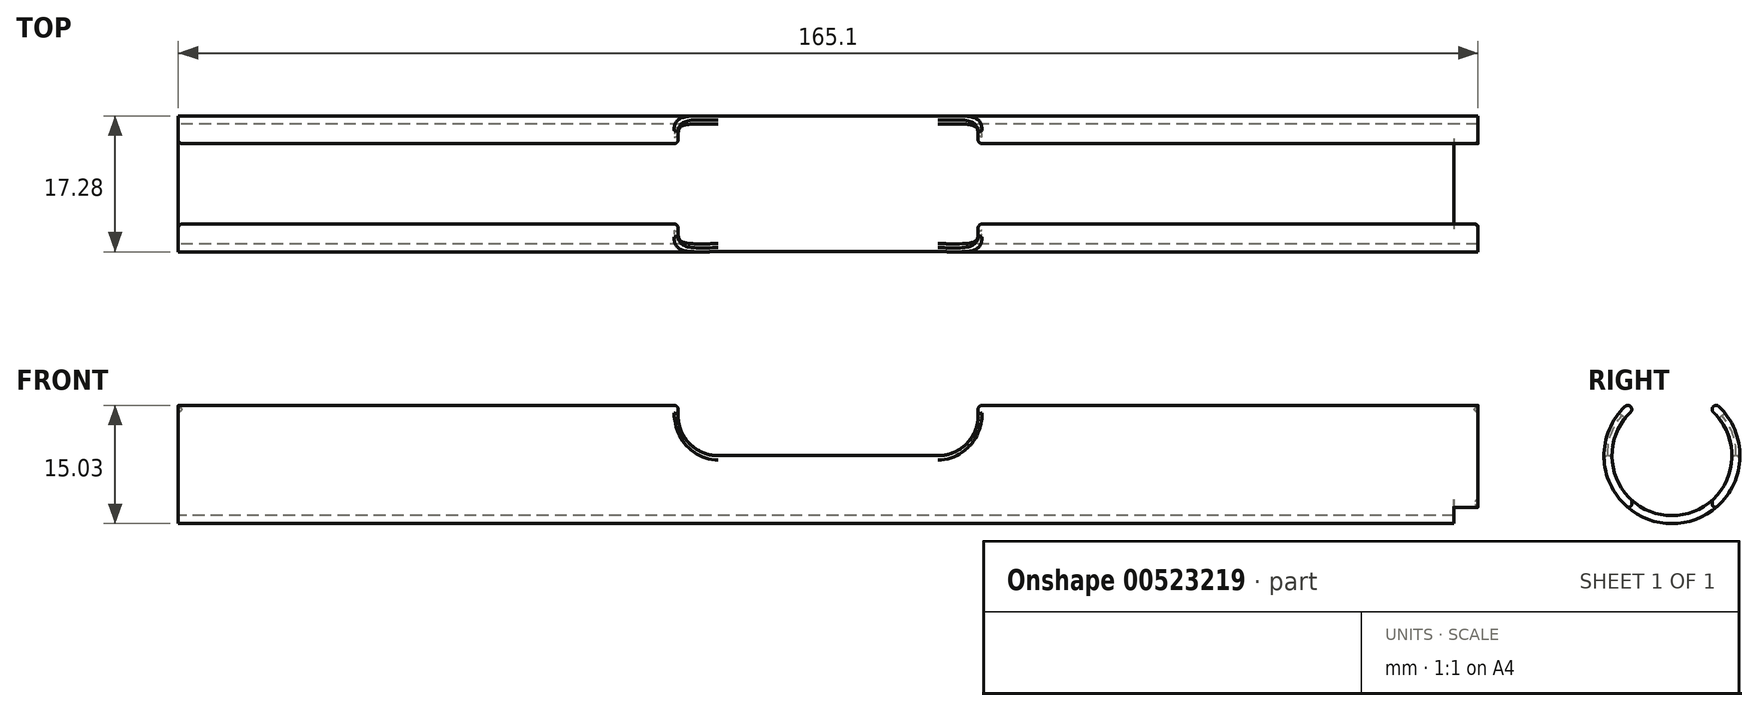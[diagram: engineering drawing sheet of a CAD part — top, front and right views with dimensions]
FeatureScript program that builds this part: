
annotation { "Feature Type Name" : "Feature", "Feature Type Description" : "" }
export const myFeature = defineFeature(function(context is Context, id is Id, definition is map)
    precondition{}
    {
        {
            var Q0;
            Q0=qCreatedBy(makeId("Right.planeOp"),FACE);
            var sketch = newSketch(context, id + "F0", { "sketchPlane" : qUnion([Q0])});
            skArc(sketch, "E0", {"start": v(-5.1, 6.97) * mm, "mid": v(0, -8.64) * mm, "end": v(5.1, 6.97) * mm});
            skArc(sketch, "E1", {"start": v(-5.1, 5.66) * mm, "mid": v(0, -7.62) * mm, "end": v(5.1, 5.66) * mm});
            skLineSegment(sketch, "E2", {"start": v(-5.1, 6.97) * mm, "end": v(-5.1, 5.66) * mm});
            skLineSegment(sketch, "E3", {"start": v(5.1, 6.97) * mm, "end": v(5.1, 5.66) * mm});
            skSolve(sketch);
        }
        {
            var Q0;
            Q0=makeQuery(id+"F0.imprint","IMPRINT",FACE,{"disambiguationData":[TD([[makeQuery(id+"F0.imprint","IMPRINT",EDGE,{"derivedFrom":sQuery(id+"F0.wireOp",EDGE,"E0")}),1.0]])]});
            extrude(context, id + "F1", {"entities" : qUnion([Q0]), "depth" : 165.1 * mm, "offsetDistance" : 25.4 * mm});
        }
        {
            var Q0;
            Q0=qCreatedBy(makeId("Front.planeOp"),FACE);
            var sketch = newSketch(context, id + "F2", { "sketchPlane" : qUnion([Q0])});
            skLineSegment(sketch, "E4", {"start": v(63.5, 8.64) * mm, "end": v(63.5, 0) * mm});
            skLineSegment(sketch, "E5", {"start": v(101.6, 8.64) * mm, "end": v(101.6, 0) * mm});
            skLineSegment(sketch, "E6", {"start": v(63.5, 8.64) * mm, "end": v(101.6, 8.64) * mm});
            skPoint(sketch, "E7.orphan", {"position": v(104.85, 8.64) * mm});
            skPoint(sketch, "E8.orphan", {"position": v(104.85, 0) * mm});
            skPoint(sketch, "E9.orphan", {"position": v(101.6, -19.63) * mm});
            skPoint(sketch, "E10.orphan", {"position": v(63.5, -19.63) * mm});
            skLineSegment(sketch, "E11", {"start": v(63.5, 0) * mm, "end": v(101.6, 0) * mm});
            skSolve(sketch);
        }
        {
            var Q0;
            Q0 = qSketchRegion(id + "F2", true);
            extrude(context, id + "F3", {"entities" : qUnion([Q0]), "operationType" : NewBodyOperationType.REMOVE, "endBound" : BoundingType.SYMMETRIC, "depth" : 25.4 * mm, "offsetDistance" : 25.4 * mm});
        }
        {
            var Q0;
            Q0=makeQuery(id+"F3.boolean.opBoolean","COPY",EDGE,{"disambiguationData":[OD(1.0)],"derivedFrom":makeQuery(id+"F3.opExtrude","SWEPT_EDGE",EDGE,{"disambiguationData":[OSD([sQuery(id+"F2.wireOp",EDGE,"E4"),sQuery(id+"F2.wireOp",EDGE,"E11")])]})});
            var Q1;
            Q1=makeQuery(id+"F3.boolean.opBoolean","COPY",EDGE,{"disambiguationData":[OD(0.0)],"derivedFrom":makeQuery(id+"F3.opExtrude","SWEPT_EDGE",EDGE,{"disambiguationData":[OSD([sQuery(id+"F2.wireOp",EDGE,"E4"),sQuery(id+"F2.wireOp",EDGE,"E11")])]})});
            var Q2;
            Q2=makeQuery(id+"F3.boolean.opBoolean","COPY",EDGE,{"disambiguationData":[OD(1.0)],"derivedFrom":makeQuery(id+"F3.opExtrude","SWEPT_EDGE",EDGE,{"disambiguationData":[OSD([sQuery(id+"F2.wireOp",EDGE,"E5"),sQuery(id+"F2.wireOp",EDGE,"E11")])]})});
            var Q3;
            Q3=makeQuery(id+"F3.boolean.opBoolean","COPY",EDGE,{"disambiguationData":[OD(0.0)],"derivedFrom":makeQuery(id+"F3.opExtrude","SWEPT_EDGE",EDGE,{"disambiguationData":[OSD([sQuery(id+"F2.wireOp",EDGE,"E5"),sQuery(id+"F2.wireOp",EDGE,"E11")])]})});
            fillet(context, id + "F4", {"entities" : qUnion([Q0, Q1, Q2, Q3]), "radius" : 5.08 * mm, "tangentPropagation" : true, "allowEdgeOverflow" : false});
        }
        {
            var Q0;
            Q0=makeQuery(id+"F3.boolean.opBoolean","INTERSECT",EDGE,{"derivedFrom":[makeQuery(id+"F1.opExtrude","SWEPT_FACE",FACE,{"disambiguationData":[OSD([sQuery(id+"F0.wireOp",EDGE,"E2")])]}),makeQuery(id+"F3.opExtrude","SWEPT_FACE",FACE,{"disambiguationData":[OSD([sQuery(id+"F2.wireOp",EDGE,"E4")])]})]});
            var Q1;
            Q1=makeQuery(id+"F3.boolean.opBoolean","INTERSECT",EDGE,{"derivedFrom":[makeQuery(id+"F1.opExtrude","SWEPT_FACE",FACE,{"disambiguationData":[OSD([sQuery(id+"F0.wireOp",EDGE,"E3")])]}),makeQuery(id+"F3.opExtrude","SWEPT_FACE",FACE,{"disambiguationData":[OSD([sQuery(id+"F2.wireOp",EDGE,"E4")])]})]});
            var Q2;
            {var subQ0=sQuery(id+"F0.wireOp",EDGE,"E2");var subQ1=sQuery(id+"F0.wireOp",EDGE,"E1");Q2=makeQuery(id+"F3.boolean.opBoolean","SPLIT",EDGE,{"disambiguationData":[TD([makeQuery(id+"F3.opExtrude","SWEPT_FACE",FACE,{"disambiguationData":[OSD([sQuery(id+"F2.wireOp",EDGE,"E4")])]})])],"derivedFrom":makeQuery(id+"F1.opExtrude","SWEPT_EDGE",EDGE,{"disambiguationData":[OSD([subQ1,subQ0])]})});}
            var Q3;
            Q3=makeQuery(id+"F1.opExtrude","CAP_EDGE",EDGE,{"disambiguationData":[OSD([sQuery(id+"F0.wireOp",EDGE,"E2")])],"isStart":true});
            var Q4;
            {var subQ0=sQuery(id+"F0.wireOp",EDGE,"E3");var subQ1=sQuery(id+"F0.wireOp",EDGE,"E1");Q4=makeQuery(id+"F3.boolean.opBoolean","SPLIT",EDGE,{"disambiguationData":[TD([makeQuery(id+"F3.opExtrude","SWEPT_FACE",FACE,{"disambiguationData":[OSD([sQuery(id+"F2.wireOp",EDGE,"E4")])]})])],"derivedFrom":makeQuery(id+"F1.opExtrude","SWEPT_EDGE",EDGE,{"disambiguationData":[OSD([subQ1,subQ0])]})});}
            var Q5;
            Q5=makeQuery(id+"F1.opExtrude","CAP_EDGE",EDGE,{"disambiguationData":[OSD([sQuery(id+"F0.wireOp",EDGE,"E3")])],"isStart":true});
            var Q6;
            {var subQ0=sQuery(id+"F0.wireOp",EDGE,"E2");var subQ1=sQuery(id+"F0.wireOp",EDGE,"E1");Q6=makeQuery(id+"F3.boolean.opBoolean","SPLIT",EDGE,{"disambiguationData":[TD([makeQuery(id+"F3.opExtrude","SWEPT_FACE",FACE,{"disambiguationData":[OSD([sQuery(id+"F2.wireOp",EDGE,"E5")])]})])],"derivedFrom":makeQuery(id+"F1.opExtrude","SWEPT_EDGE",EDGE,{"disambiguationData":[OSD([subQ1,subQ0])]})});}
            var Q7;
            Q7=makeQuery(id+"F3.boolean.opBoolean","INTERSECT",EDGE,{"derivedFrom":[makeQuery(id+"F1.opExtrude","SWEPT_FACE",FACE,{"disambiguationData":[OSD([sQuery(id+"F0.wireOp",EDGE,"E2")])]}),makeQuery(id+"F3.opExtrude","SWEPT_FACE",FACE,{"disambiguationData":[OSD([sQuery(id+"F2.wireOp",EDGE,"E5")])]})]});
            var Q8;
            Q8=makeQuery(id+"F3.boolean.opBoolean","INTERSECT",EDGE,{"derivedFrom":[makeQuery(id+"F1.opExtrude","SWEPT_FACE",FACE,{"disambiguationData":[OSD([sQuery(id+"F0.wireOp",EDGE,"E3")])]}),makeQuery(id+"F3.opExtrude","SWEPT_FACE",FACE,{"disambiguationData":[OSD([sQuery(id+"F2.wireOp",EDGE,"E5")])]})]});
            var Q9;
            {var subQ0=sQuery(id+"F0.wireOp",EDGE,"E3");var subQ1=sQuery(id+"F0.wireOp",EDGE,"E1");Q9=makeQuery(id+"F3.boolean.opBoolean","SPLIT",EDGE,{"disambiguationData":[TD([makeQuery(id+"F3.opExtrude","SWEPT_FACE",FACE,{"disambiguationData":[OSD([sQuery(id+"F2.wireOp",EDGE,"E5")])]})])],"derivedFrom":makeQuery(id+"F1.opExtrude","SWEPT_EDGE",EDGE,{"disambiguationData":[OSD([subQ1,subQ0])]})});}
            var Q10;
            Q10=makeQuery(id+"F3.boolean.opBoolean","INTERSECT",EDGE,{"disambiguationData":[OD(1.0)],"derivedFrom":[makeQuery(id+"F1.opExtrude","SWEPT_FACE",FACE,{"disambiguationData":[OSD([sQuery(id+"F0.wireOp",EDGE,"E1")])]}),makeQuery(id+"F3.opExtrude","SWEPT_FACE",FACE,{"disambiguationData":[OSD([sQuery(id+"F2.wireOp",EDGE,"E5")])]})]});
            var Q11;
            Q11=makeQuery(id+"F1.opExtrude","CAP_EDGE",EDGE,{"disambiguationData":[OSD([sQuery(id+"F0.wireOp",EDGE,"E2")])],"isStart":false});
            var Q12;
            Q12=makeQuery(id+"F1.opExtrude","CAP_EDGE",EDGE,{"disambiguationData":[OSD([sQuery(id+"F0.wireOp",EDGE,"E3")])],"isStart":false});
            var Q13;
            {var subQ0=sQuery(id+"F0.wireOp",EDGE,"E0");var subQ1=sQuery(id+"F0.wireOp",EDGE,"E2");Q13=makeQuery(id+"F3.boolean.opBoolean","SPLIT",EDGE,{"disambiguationData":[TD([makeQuery(id+"F3.opExtrude","SWEPT_FACE",FACE,{"disambiguationData":[OSD([sQuery(id+"F2.wireOp",EDGE,"E5")])]})])],"derivedFrom":makeQuery(id+"F1.opExtrude","SWEPT_EDGE",EDGE,{"disambiguationData":[OSD([subQ0,subQ1])]})});}
            var Q14;
            {var subQ0=sQuery(id+"F0.wireOp",EDGE,"E0");var subQ1=sQuery(id+"F0.wireOp",EDGE,"E3");Q14=makeQuery(id+"F3.boolean.opBoolean","SPLIT",EDGE,{"disambiguationData":[TD([makeQuery(id+"F3.opExtrude","SWEPT_FACE",FACE,{"disambiguationData":[OSD([sQuery(id+"F2.wireOp",EDGE,"E5")])]})])],"derivedFrom":makeQuery(id+"F1.opExtrude","SWEPT_EDGE",EDGE,{"disambiguationData":[OSD([subQ0,subQ1])]})});}
            var Q15;
            Q15=makeQuery(id+"F3.boolean.opBoolean","INTERSECT",EDGE,{"disambiguationData":[OD(0.0)],"derivedFrom":[makeQuery(id+"F1.opExtrude","SWEPT_FACE",FACE,{"disambiguationData":[OSD([sQuery(id+"F0.wireOp",EDGE,"E1")])]}),makeQuery(id+"F3.opExtrude","SWEPT_FACE",FACE,{"disambiguationData":[OSD([sQuery(id+"F2.wireOp",EDGE,"E5")])]})]});
            var Q16;
            {var subQ0=sQuery(id+"F0.wireOp",EDGE,"E0");var subQ1=sQuery(id+"F0.wireOp",EDGE,"E2");Q16=makeQuery(id+"F3.boolean.opBoolean","SPLIT",EDGE,{"disambiguationData":[TD([makeQuery(id+"F3.opExtrude","SWEPT_FACE",FACE,{"disambiguationData":[OSD([sQuery(id+"F2.wireOp",EDGE,"E4")])]})])],"derivedFrom":makeQuery(id+"F1.opExtrude","SWEPT_EDGE",EDGE,{"disambiguationData":[OSD([subQ0,subQ1])]})});}
            var Q17;
            Q17=makeQuery(id+"F3.boolean.opBoolean","INTERSECT",EDGE,{"disambiguationData":[OD(0.0)],"derivedFrom":[makeQuery(id+"F1.opExtrude","SWEPT_FACE",FACE,{"disambiguationData":[OSD([sQuery(id+"F0.wireOp",EDGE,"E0")])]}),makeQuery(id+"F3.opExtrude","SWEPT_FACE",FACE,{"disambiguationData":[OSD([sQuery(id+"F2.wireOp",EDGE,"E4")])]})]});
            var Q18;
            {var subQ0=sQuery(id+"F0.wireOp",EDGE,"E0");var subQ1=sQuery(id+"F0.wireOp",EDGE,"E3");Q18=makeQuery(id+"F3.boolean.opBoolean","SPLIT",EDGE,{"disambiguationData":[TD([makeQuery(id+"F3.opExtrude","SWEPT_FACE",FACE,{"disambiguationData":[OSD([sQuery(id+"F2.wireOp",EDGE,"E4")])]})])],"derivedFrom":makeQuery(id+"F1.opExtrude","SWEPT_EDGE",EDGE,{"disambiguationData":[OSD([subQ0,subQ1])]})});}
            var Q19;
            Q19=makeQuery(id+"F3.boolean.opBoolean","INTERSECT",EDGE,{"disambiguationData":[OD(1.0)],"derivedFrom":[makeQuery(id+"F1.opExtrude","SWEPT_FACE",FACE,{"disambiguationData":[OSD([sQuery(id+"F0.wireOp",EDGE,"E0")])]}),makeQuery(id+"F3.opExtrude","SWEPT_FACE",FACE,{"disambiguationData":[OSD([sQuery(id+"F2.wireOp",EDGE,"E4")])]})]});
            fillet(context, id + "F5", {"entities" : qUnion([Q0, Q1, Q2, Q3, Q4, Q5, Q6, Q7, Q8, Q9, Q10, Q11, Q12, Q13, Q14, Q15, Q16, Q17, Q18, Q19]), "radius" : 0.5 * mm, "tangentPropagation" : true, "allowEdgeOverflow" : false});
        }
        {
            var Q0;
            Q0=qCreatedBy(makeId("Top.planeOp"),FACE);
            var sketch = newSketch(context, id + "F6", { "sketchPlane" : qUnion([Q0])});
            skLineSegment(sketch, "E12", {"start": v(165.1, 5.1) * mm, "end": v(165.1, -5.1) * mm});
            skLineSegment(sketch, "E13", {"start": v(162.05, 5.1) * mm, "end": v(162.05, -5.1) * mm});
            skLineSegment(sketch, "E14", {"start": v(162.05, 5.1) * mm, "end": v(165.1, 5.1) * mm});
            skLineSegment(sketch, "E15", {"start": v(162.05, -5.1) * mm, "end": v(165.1, -5.1) * mm});
            skSolve(sketch);
        }
        {
            var Q0;
            Q0 = qSketchRegion(id + "F6", true);
            extrude(context, id + "F7", {"entities" : qUnion([Q0]), "operationType" : NewBodyOperationType.REMOVE, "endBound" : BoundingType.THROUGH_ALL, "oppositeDirection" : true, "depth" : 25.4 * mm, "offsetDistance" : 25.4 * mm});
        }
        {
            var Q0;
            Q0=makeQuery(id+"F7.boolean.opBoolean","COPY",EDGE,{"derivedFrom":makeQuery(id+"F7.opExtrude","SWEPT_EDGE",EDGE,{"disambiguationData":[OSD([sQuery(id+"F6.wireOp",EDGE,"E12"),sQuery(id+"F6.wireOp",EDGE,"E14")])]})});
            var Q1;
            Q1=makeQuery(id+"F7.boolean.opBoolean","INTERSECT",EDGE,{"derivedFrom":[makeQuery(id+"F1.opExtrude","SWEPT_FACE",FACE,{"disambiguationData":[OSD([sQuery(id+"F0.wireOp",EDGE,"E1")])]}),makeQuery(id+"F7.opExtrude","SWEPT_FACE",FACE,{"disambiguationData":[OSD([sQuery(id+"F6.wireOp",EDGE,"E14")])]})]});
            var Q2;
            Q2=makeQuery(id+"F7.boolean.opBoolean","INTERSECT",EDGE,{"derivedFrom":[makeQuery(id+"F1.opExtrude","SWEPT_FACE",FACE,{"disambiguationData":[OSD([sQuery(id+"F0.wireOp",EDGE,"E1")])]}),makeQuery(id+"F7.opExtrude","SWEPT_FACE",FACE,{"disambiguationData":[OSD([sQuery(id+"F6.wireOp",EDGE,"E15")])]})]});
            var Q3;
            Q3=makeQuery(id+"F7.boolean.opBoolean","COPY",EDGE,{"derivedFrom":makeQuery(id+"F7.opExtrude","SWEPT_EDGE",EDGE,{"disambiguationData":[OSD([sQuery(id+"F6.wireOp",EDGE,"E12"),sQuery(id+"F6.wireOp",EDGE,"E15")])]})});
            var Q4;
            Q4=makeQuery(id+"F7.boolean.opBoolean","INTERSECT",EDGE,{"derivedFrom":[makeQuery(id+"F1.opExtrude","SWEPT_FACE",FACE,{"disambiguationData":[OSD([sQuery(id+"F0.wireOp",EDGE,"E0")])]}),makeQuery(id+"F7.opExtrude","SWEPT_FACE",FACE,{"disambiguationData":[OSD([sQuery(id+"F6.wireOp",EDGE,"E14")])]})]});
            var Q5;
            Q5=makeQuery(id+"F7.boolean.opBoolean","INTERSECT",EDGE,{"derivedFrom":[makeQuery(id+"F1.opExtrude","SWEPT_FACE",FACE,{"disambiguationData":[OSD([sQuery(id+"F0.wireOp",EDGE,"E0")])]}),makeQuery(id+"F7.opExtrude","SWEPT_FACE",FACE,{"disambiguationData":[OSD([sQuery(id+"F6.wireOp",EDGE,"E15")])]})]});
            fillet(context, id + "F8", {"entities" : qUnion([Q0, Q1, Q2, Q3, Q4, Q5]), "radius" : 0.38 * mm, "tangentPropagation" : true, "allowEdgeOverflow" : false});
        }
    });
